# Revit family: Louver_XAV-545_All-Lite
name_source: partatom
category: Mechanical Equipment
revit_build: Autodesk Revit 2013 (Build: 20120221_2030(x64)
units: mm (PartAtom-declared; Revit-internal decimal feet)

## types (1)
- XAV-545
    04 CSI = 08 91 00
    95 CSI = 10200
    Air Volume Delivered @ Beginning Point of Water Penetration = 4385 cfm
    Assembly Code = B2010300
    Blade Width = 2' - 11 1/2"
    Blades = Inverted V, 1/4''
    Default Height = 4' - 0"
    Design Load = 300 psf
    Flange = 5 1/2'' on top and bottom
    Frame = 5 1/2'' deep x .25'' thick
    Free Area = [48'' x 48'' unit] : 7.9 ft² 49%
    Free Area Velocity @ Beginning Point of Water Penetration = 555 fpm
    Height = 4' - 0"
    Height Control = 4' - 0"
    Louver = Aluminum
    Louver Count = 22
    Manufacturer = All-Lite
    Max Height = 8' - 0"
    Max Width = 10' - 0"
    Maximum Size - Multiple Section = Unlimited width x single section high, Single section wide x unlimited height
    Maximum Size - Single Section = 60'' x 120'', 120'' x 60''
    Min Height = 0' - 6"
    Min Width = 0' - 6"
    Minimum Size = 12'' x 12''
    Model = XAV-545
    Mullion = Visible
    Omni Class Code = 23-60 11 17
    Omni Class Title = Exterior Louvers & Grilles
    Pressure Loss @ Beginning Point of Water Penetration = 0.094 in. wg.
    Product URL = http://www.alllite.com
    Screen = 1/2'' x .063'' expanded and flattened stainless steel
    Screen Frame = Removable
    URL = http://alllite.com
    Velocity @ .15 in. wg Pressure Loss = 755 fpm
    Warranty = http://www.alllite.com
    Width = 3' - 0"
    Width Control = 3' - 0"

## geometry (parser evidence)
native form markers: Blend x6, Sweep x5
no freeform markers — native parametric forms only
